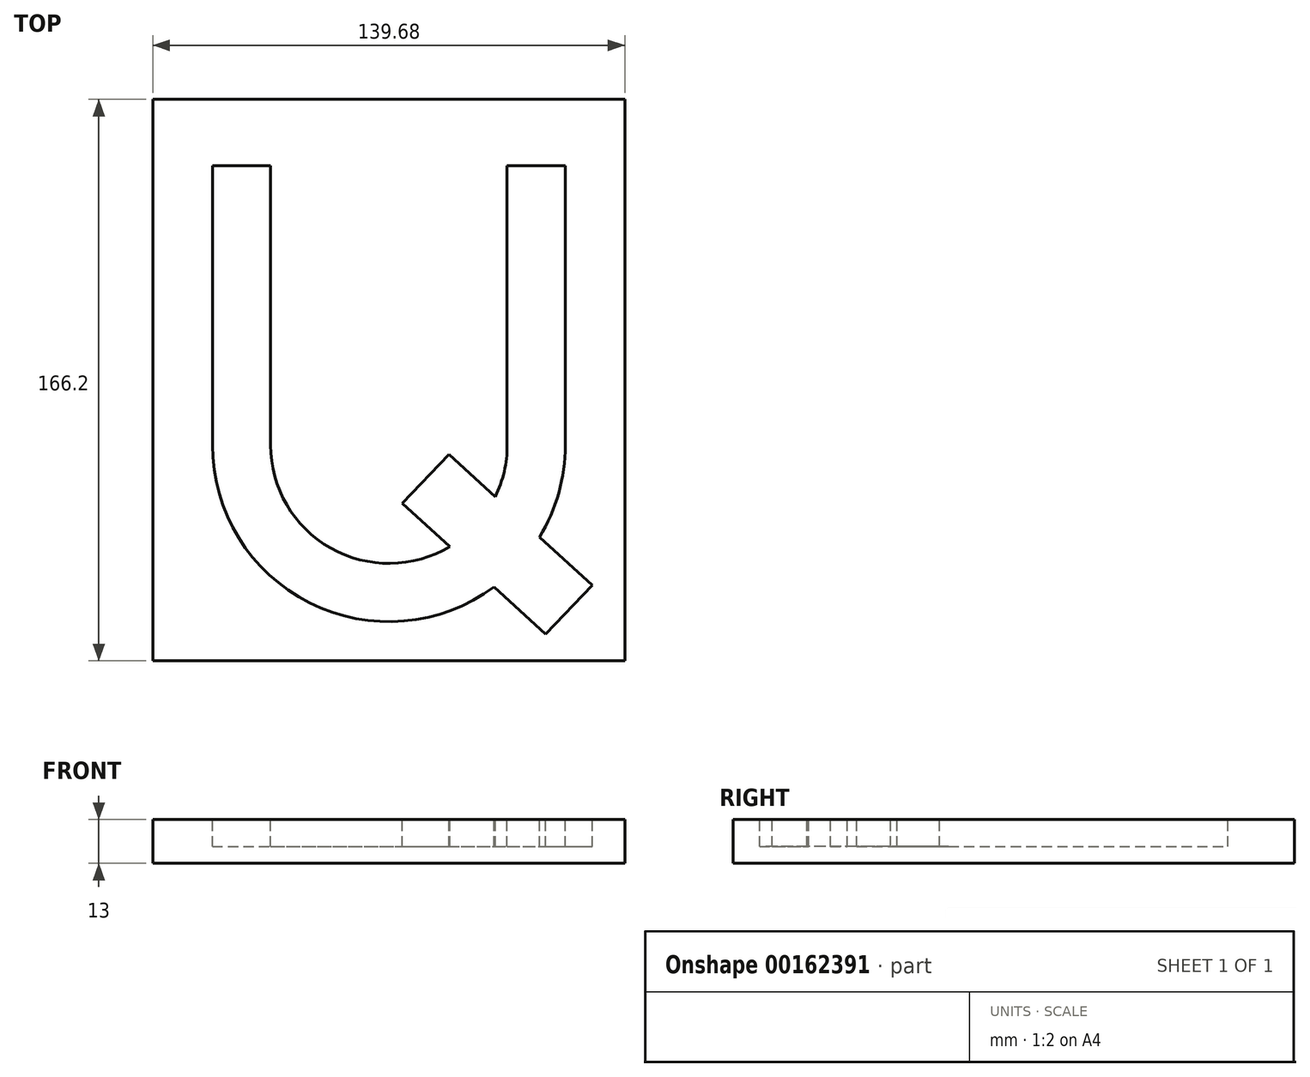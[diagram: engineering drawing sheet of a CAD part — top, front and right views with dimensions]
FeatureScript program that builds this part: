
annotation { "Feature Type Name" : "Feature", "Feature Type Description" : "" }
export const myFeature = defineFeature(function(context is Context, id is Id, definition is map)
    precondition{}
    {
        {
            var Q0;
            Q0=qCreatedBy(makeId("Top.planeOp"),FACE);
            var sketch = newSketch(context, id + "F0", { "sketchPlane" : qUnion([Q0])});
            skLineSegment(sketch, "E0", {"start": v(-69.84, 83.1) * mm, "end": v(-69.84, -83.1) * mm});
            skLineSegment(sketch, "E1", {"start": v(-69.84, -83.1) * mm, "end": v(69.84, -83.1) * mm});
            skLineSegment(sketch, "E2", {"start": v(69.84, 83.1) * mm, "end": v(69.84, -83.1) * mm});
            skLineSegment(sketch, "E3", {"start": v(-69.84, 83.1) * mm, "end": v(69.84, 83.1) * mm});
            skSolve(sketch);
        }
        {
            var Q0;
            Q0=makeQuery(id+"F0.imprint","IMPRINT",FACE,{"disambiguationData":[TD([[makeQuery(id+"F0.imprint","IMPRINT",EDGE,{"derivedFrom":sQuery(id+"F0.wireOp",EDGE,"E0")}),1.0]])]});
            extrude(context, id + "F1", {"entities" : qUnion([Q0]), "depth" : 13 * mm});
        }
        {
            var Q0;
            Q0=makeQuery(id+"F1.opExtrude","CAP_FACE",FACE,{"disambiguationData":[OSD([sQuery(id+"F0.wireOp",EDGE,"E0"),sQuery(id+"F0.wireOp",EDGE,"E1"),sQuery(id+"F0.wireOp",EDGE,"E2"),sQuery(id+"F0.wireOp",EDGE,"E3")])],"isStart":false});
            var sketch = newSketch(context, id + "F2", { "sketchPlane" : qUnion([Q0])});
            skLineSegment(sketch, "E4", {"start": v(-52.22, -19.3) * mm, "end": v(-52.22, 63.41) * mm});
            skArc(sketch, "E5", {"start": v(-52.22, -19.3) * mm, "mid": v(-23.49, -65.94) * mm, "end": v(31.1, -61.25) * mm});
            skLineSegment(sketch, "E6", {"start": v(52.22, -19.3) * mm, "end": v(52.22, 63.41) * mm});
            skLineSegment(sketch, "E7", {"start": v(-52.22, 63.41) * mm, "end": v(-35, 63.41) * mm});
            skLineSegment(sketch, "E8", {"start": v(-35, -19.3) * mm, "end": v(-35, 63.41) * mm});
            skArc(sketch, "E9", {"start": v(-35, -19.3) * mm, "mid": v(-17.24, -49.76) * mm, "end": v(18.02, -49.3) * mm});
            skLineSegment(sketch, "E10", {"start": v(35, -19.3) * mm, "end": v(35, 63.41) * mm});
            skLineSegment(sketch, "E11", {"start": v(35, 63.41) * mm, "end": v(52.22, 63.41) * mm});
            skLineSegment(sketch, "E12", {"start": v(17.82, -22.03) * mm, "end": v(31.5, -34.54) * mm});
            skLineSegment(sketch, "E13", {"start": v(4, -36.5) * mm, "end": v(18.02, -49.3) * mm});
            skLineSegment(sketch, "E14", {"start": v(4, -36.5) * mm, "end": v(17.82, -22.03) * mm});
            skLineSegment(sketch, "E15", {"start": v(46.41, -75.24) * mm, "end": v(60.22, -60.77) * mm});
            skArc(sketch, "E16", {"start": v(44.59, -46.49) * mm, "mid": v(50.28, -33.42) * mm, "end": v(52.22, -19.3) * mm});
            skArc(sketch, "E17", {"start": v(31.5, -34.54) * mm, "mid": v(34.12, -27.11) * mm, "end": v(35, -19.3) * mm});
            skLineSegment(sketch, "E18", {"start": v(44.59, -46.49) * mm, "end": v(60.22, -60.77) * mm});
            skLineSegment(sketch, "E19", {"start": v(31.1, -61.25) * mm, "end": v(46.41, -75.24) * mm});
            skSolve(sketch);
        }
        {
            var Q0;
            Q0=makeQuery(id+"F2.imprint","IMPRINT",FACE,{"disambiguationData":[TD([[makeQuery(id+"F2.imprint","IMPRINT",EDGE,{"derivedFrom":sQuery(id+"F2.wireOp",EDGE,"E4")}),-1.0]])]});
            extrude(context, id + "F3", {"entities" : qUnion([Q0]), "operationType" : NewBodyOperationType.REMOVE, "oppositeDirection" : true, "depth" : 8 * mm});
        }
    });
